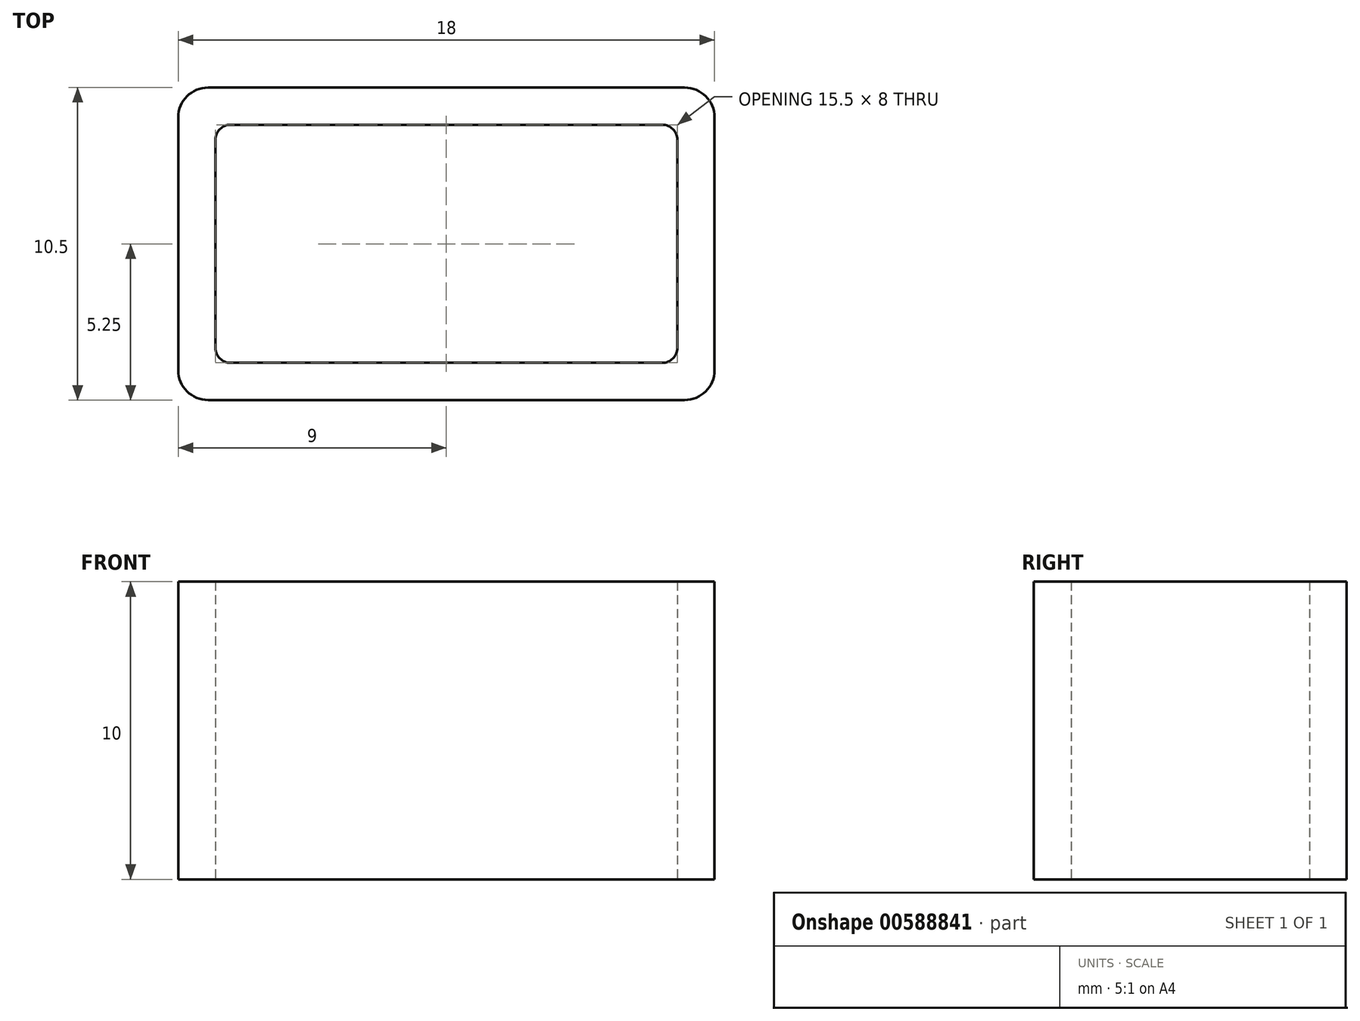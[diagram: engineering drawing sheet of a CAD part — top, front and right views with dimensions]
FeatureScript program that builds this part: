
annotation { "Feature Type Name" : "Feature", "Feature Type Description" : "" }
export const myFeature = defineFeature(function(context is Context, id is Id, definition is map)
    precondition{}
    {
        {
            var Q0;
            Q0=qCreatedBy(makeId("Top.planeOp"),FACE);
            var sketch = newSketch(context, id + "F0", { "sketchPlane" : qUnion([Q0])});
            skLineSegment(sketch, "E0.bottom", {"start": v(7.25, -4) * mm, "end": v(-7.25, -4) * mm});
            skLineSegment(sketch, "E0.top", {"start": v(7.25, 4) * mm, "end": v(-7.25, 4) * mm});
            skLineSegment(sketch, "E0.left", {"start": v(7.75, -3.5) * mm, "end": v(7.75, 3.5) * mm});
            skLineSegment(sketch, "E0.right", {"start": v(-7.75, -3.5) * mm, "end": v(-7.75, 3.5) * mm});
            skPoint(sketch, "E0.middle", {"position": v(0, 0) * mm});
            skLineSegment(sketch, "E1.bottom", {"start": v(8, -5.25) * mm, "end": v(-8, -5.25) * mm});
            skLineSegment(sketch, "E1.top", {"start": v(8, 5.25) * mm, "end": v(-8, 5.25) * mm});
            skLineSegment(sketch, "E1.left", {"start": v(9, -4.25) * mm, "end": v(9, 4.25) * mm});
            skLineSegment(sketch, "E1.right", {"start": v(-9, -4.25) * mm, "end": v(-9, 4.25) * mm});
            skPoint(sketch, "E2.visualSharp", {"position": v(-7.75, 4) * mm});
            skArc(sketch, "E2.filletArc", {"start": v(-7.25, 4) * mm, "mid": v(-7.6, 3.85) * mm, "end": v(-7.75, 3.5) * mm});
            skPoint(sketch, "E3.visualSharp", {"position": v(7.75, 4) * mm});
            skArc(sketch, "E3.filletArc", {"start": v(7.75, 3.5) * mm, "mid": v(7.6, 3.85) * mm, "end": v(7.25, 4) * mm});
            skPoint(sketch, "E4.visualSharp", {"position": v(7.75, -4) * mm});
            skArc(sketch, "E4.filletArc", {"start": v(7.25, -4) * mm, "mid": v(7.6, -3.85) * mm, "end": v(7.75, -3.5) * mm});
            skPoint(sketch, "E5.visualSharp", {"position": v(-7.75, -4) * mm});
            skArc(sketch, "E5.filletArc", {"start": v(-7.75, -3.5) * mm, "mid": v(-7.6, -3.85) * mm, "end": v(-7.25, -4) * mm});
            skPoint(sketch, "E6.visualSharp", {"position": v(-9, 5.25) * mm});
            skArc(sketch, "E6.filletArc", {"start": v(-8, 5.25) * mm, "mid": v(-8.7, 4.96) * mm, "end": v(-9, 4.25) * mm});
            skPoint(sketch, "E7.visualSharp", {"position": v(9, 5.25) * mm});
            skArc(sketch, "E7.filletArc", {"start": v(9, 4.25) * mm, "mid": v(8.7, 4.96) * mm, "end": v(8, 5.25) * mm});
            skPoint(sketch, "E8.visualSharp", {"position": v(9, -5.25) * mm});
            skArc(sketch, "E8.filletArc", {"start": v(8, -5.25) * mm, "mid": v(8.7, -4.96) * mm, "end": v(9, -4.25) * mm});
            skPoint(sketch, "E9.visualSharp", {"position": v(-9, -5.25) * mm});
            skArc(sketch, "E9.filletArc", {"start": v(-9, -4.25) * mm, "mid": v(-8.7, -4.96) * mm, "end": v(-8, -5.25) * mm});
            skSolve(sketch);
        }
        {
            var Q0;
            Q0=makeQuery(id+"F0.imprint","IMPRINT",FACE,{"disambiguationData":[TD([[makeQuery(id+"F0.imprint","IMPRINT",EDGE,{"derivedFrom":sQuery(id+"F0.wireOp",EDGE,"E0.bottom")}),1.0]])]});
            extrude(context, id + "F1", {"entities" : qUnion([Q0]), "depth" : 10 * mm, "offsetDistance" : 25 * mm});
        }
    });
